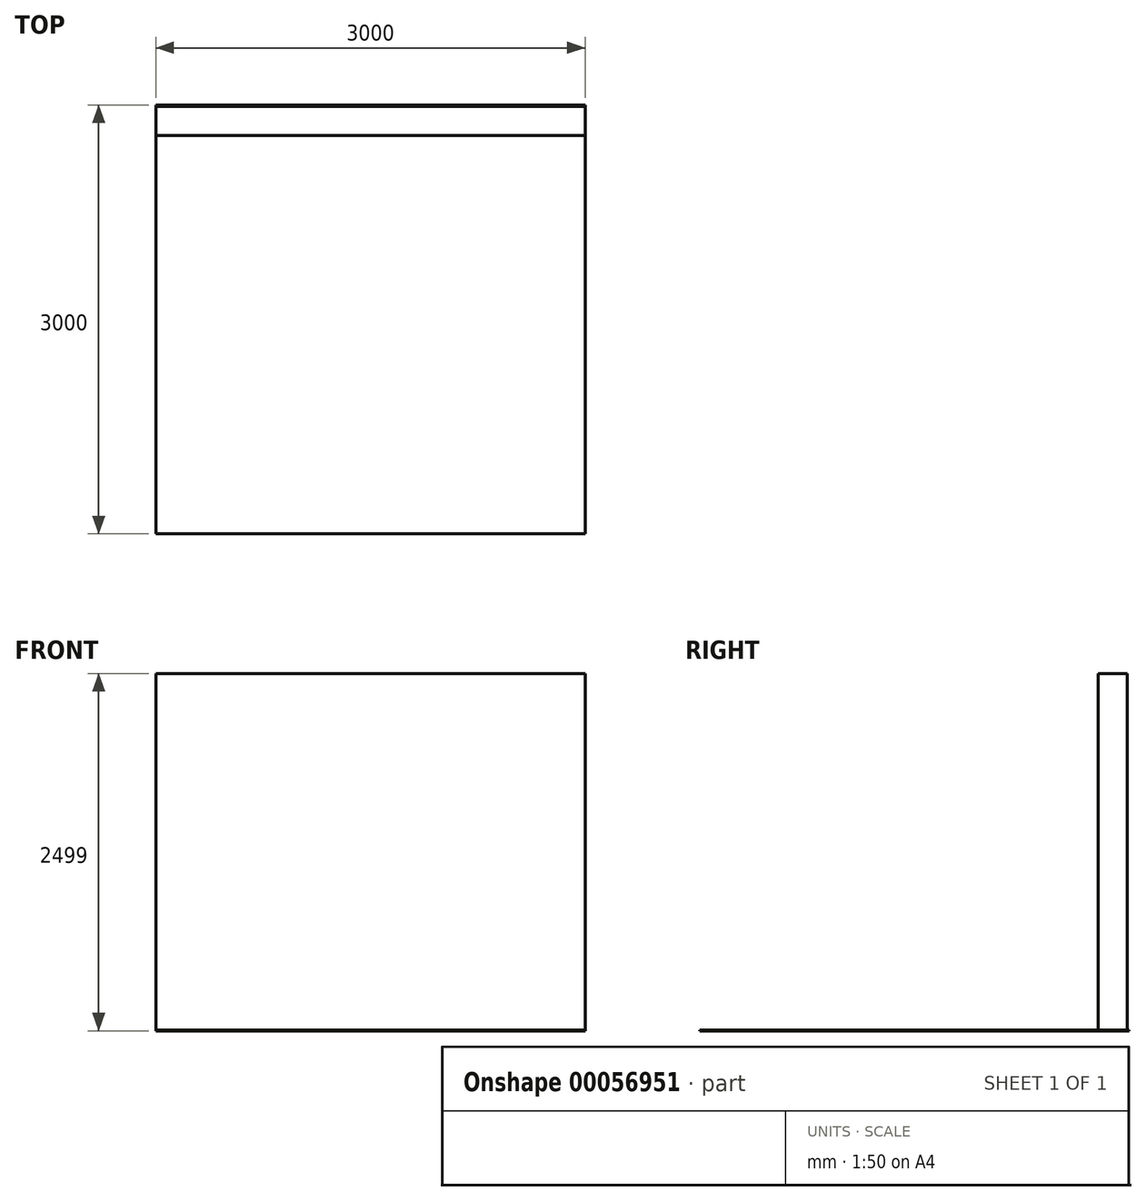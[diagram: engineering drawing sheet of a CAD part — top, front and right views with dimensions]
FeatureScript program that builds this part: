
annotation { "Feature Type Name" : "Feature", "Feature Type Description" : "" }
export const myFeature = defineFeature(function(context is Context, id is Id, definition is map)
    precondition{}
    {
        {
            var Q0;
            Q0=qCreatedBy(makeId("Top.planeOp"),FACE);
            var sketch = newSketch(context, id + "F0", { "sketchPlane" : qUnion([Q0])});
            skLineSegment(sketch, "E0.bottom", {"start": v(0, 0) * mm, "end": v(-3000, 0) * mm});
            skLineSegment(sketch, "E0.top", {"start": v(0, -3000) * mm, "end": v(-3000, -3000) * mm});
            skLineSegment(sketch, "E0.left", {"start": v(0, 0) * mm, "end": v(0, -3000) * mm});
            skLineSegment(sketch, "E0.right", {"start": v(-3000, 0) * mm, "end": v(-3000, -3000) * mm});
            skSolve(sketch);
        }
        {
            var Q0;
            Q0=makeQuery(id+"F0.imprint","IMPRINT",FACE,{"disambiguationData":[TD([[makeQuery(id+"F0.imprint","IMPRINT",EDGE,{"derivedFrom":sQuery(id+"F0.wireOp",EDGE,"E0.bottom")}),1.0]])]});
            extrude(context, id + "F1", {"entities" : qUnion([Q0]), "depth" : 4 * mm, "offsetDistance" : 25 * mm});
        }
        {
            var Q0;
            Q0=makeQuery(id+"F1.opExtrude","CAP_FACE",FACE,{"disambiguationData":[OSD([sQuery(id+"F0.wireOp",EDGE,"E0.bottom"),sQuery(id+"F0.wireOp",EDGE,"E0.top"),sQuery(id+"F0.wireOp",EDGE,"E0.left"),sQuery(id+"F0.wireOp",EDGE,"E0.right")])],"isStart":false});
            var sketch = newSketch(context, id + "F2", { "sketchPlane" : qUnion([Q0])});
            skLineSegment(sketch, "E1.bottom", {"start": v(-3000, -10) * mm, "end": v(0, -10) * mm});
            skLineSegment(sketch, "E1.top", {"start": v(-3000, -215) * mm, "end": v(0, -215) * mm});
            skLineSegment(sketch, "E1.left", {"start": v(-3000, -10) * mm, "end": v(-3000, -215) * mm});
            skLineSegment(sketch, "E1.right", {"start": v(0, -10) * mm, "end": v(0, -215) * mm});
            skSolve(sketch);
        }
        {
            var Q0;
            Q0 = qSketchRegion(id + "F2", true);
            extrude(context, id + "F3", {"entities" : qUnion([Q0]), "depth" : 2495 * mm, "offsetDistance" : 25 * mm});
        }
    });
